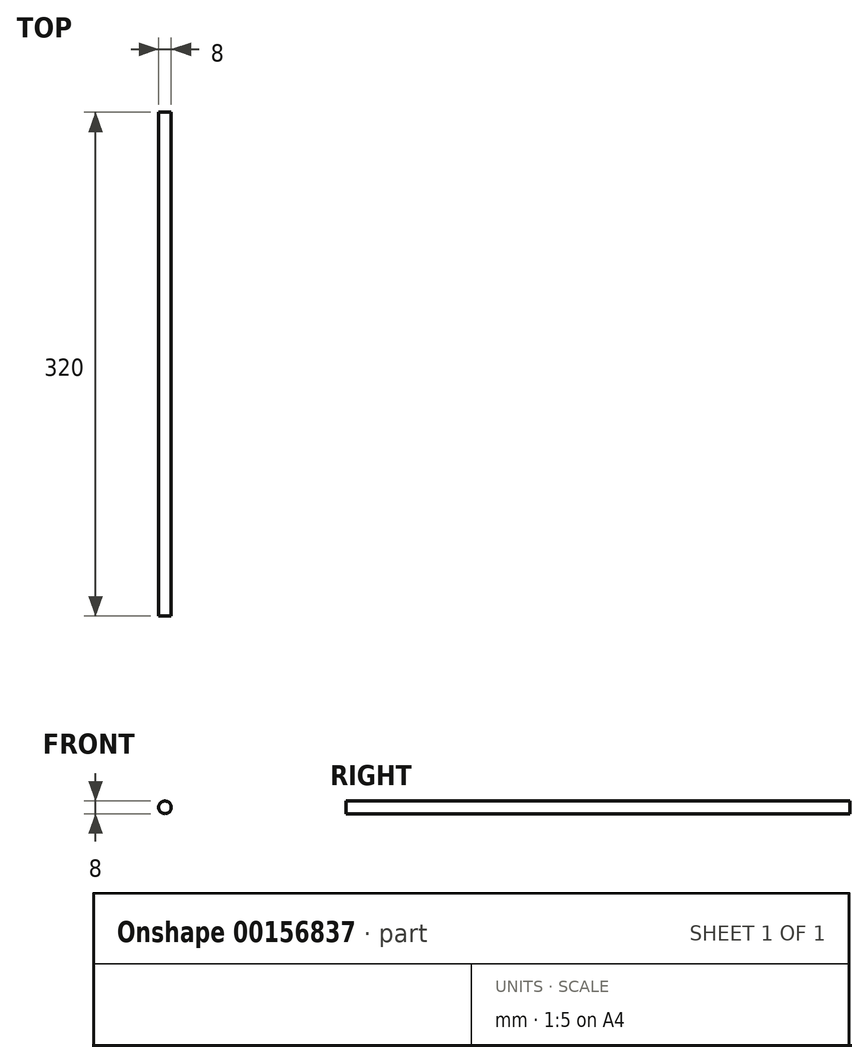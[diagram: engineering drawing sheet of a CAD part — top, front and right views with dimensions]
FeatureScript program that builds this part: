
annotation { "Feature Type Name" : "Feature", "Feature Type Description" : "" }
export const myFeature = defineFeature(function(context is Context, id is Id, definition is map)
    precondition{}
    {
        {
            var Q0;
            Q0=qCreatedBy(makeId("Front.planeOp"),FACE);
            var sketch = newSketch(context, id + "F0", { "sketchPlane" : qUnion([Q0])});
            skCircle(sketch, "E0", {"center": v(0, 0) * mm, "radius": 4 * mm});
            skSolve(sketch);
        }
        {
            var Q0;
            Q0=qSketchRegion(id+"F0",true);
            extrude(context, id + "F1", {"entities" : qUnion([Q0]), "endBound" : BoundingType.SYMMETRIC, "depth" : 320 * mm});
        }
    });
